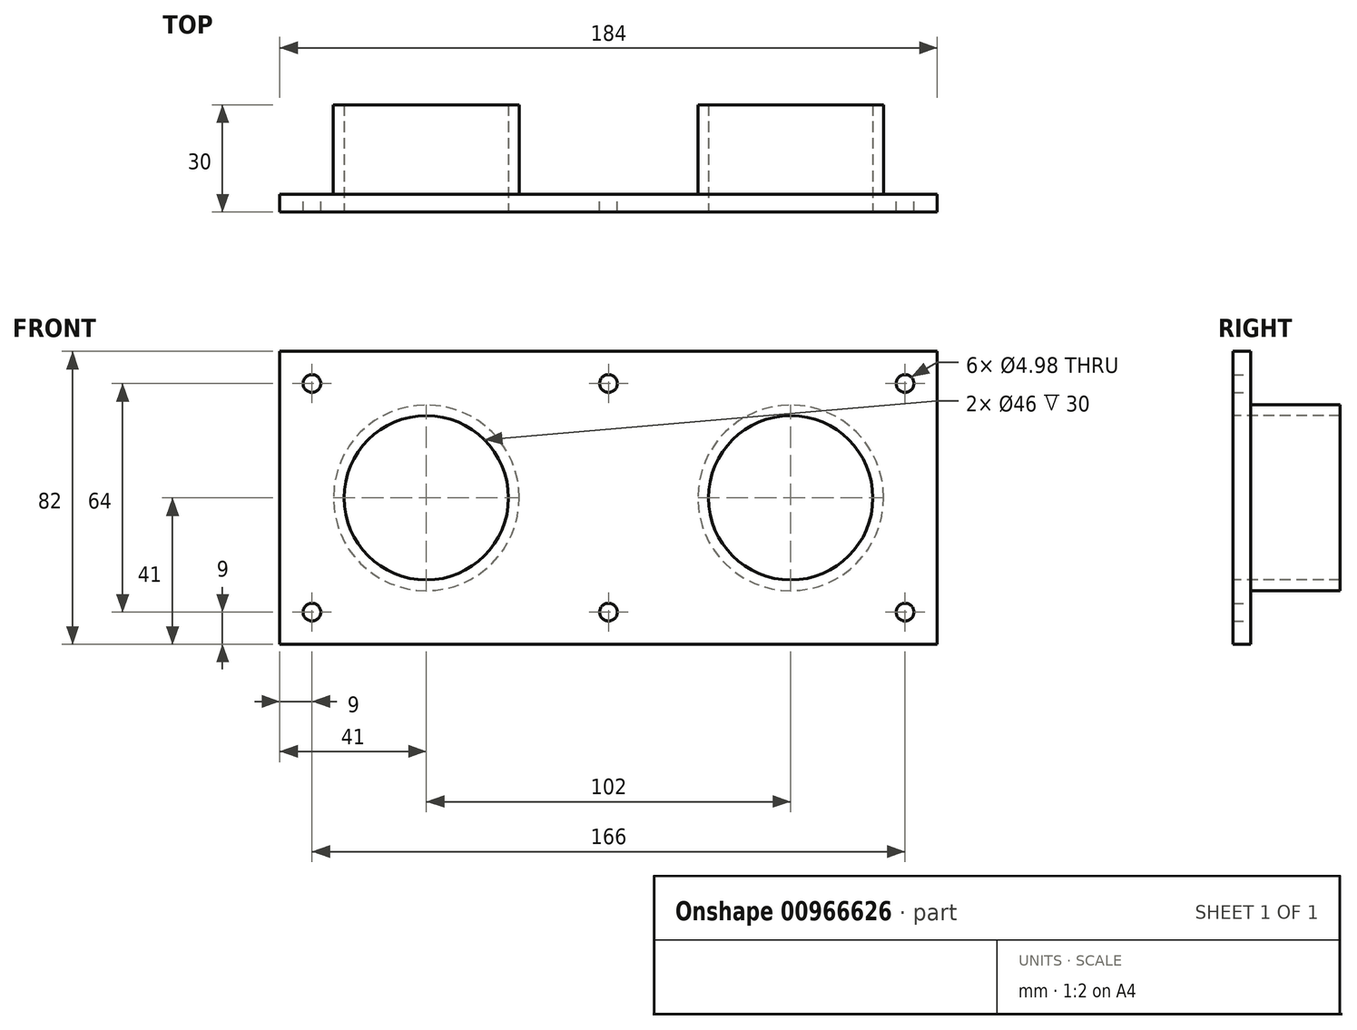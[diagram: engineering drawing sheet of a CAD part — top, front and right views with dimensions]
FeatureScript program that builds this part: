
annotation { "Feature Type Name" : "Feature", "Feature Type Description" : "" }
export const myFeature = defineFeature(function(context is Context, id is Id, definition is map)
    precondition{}
    {
        {
            var Q0;
            Q0=qCreatedBy(makeId("Front.planeOp"),FACE);
            var sketch = newSketch(context, id + "F0", { "sketchPlane" : qUnion([Q0])});
            skCircle(sketch, "E0", {"center": v(-51, 0) * mm, "radius": 26 * mm});
            skCircle(sketch, "E1", {"center": v(51, 0) * mm, "radius": 26 * mm});
            skLineSegment(sketch, "E2", {"start": v(-25, 0) * mm, "end": v(25, 0) * mm, "construction": true});
            skPoint(sketch, "E3", {"position": v(0, 0) * mm});
            skLineSegment(sketch, "E4", {"start": v(-92, 41) * mm, "end": v(-92, -41) * mm});
            skLineSegment(sketch, "E5", {"start": v(-92, -41) * mm, "end": v(92, -41) * mm});
            skLineSegment(sketch, "E6", {"start": v(92, -41) * mm, "end": v(92, 41) * mm});
            skLineSegment(sketch, "E7", {"start": v(92, 41) * mm, "end": v(-92, 41) * mm});
            skCircle(sketch, "E8.0", {"center": v(-51, 0) * mm, "radius": 23 * mm});
            skCircle(sketch, "E9.0", {"center": v(51, 0) * mm, "radius": 23 * mm});
            skSolve(sketch);
        }
        {
            var Q0;
            Q0=makeQuery(id+"F0.imprint","IMPRINT",FACE,{"disambiguationData":[TD([[makeQuery(id+"F0.imprint","IMPRINT",EDGE,{"derivedFrom":sQuery(id+"F0.wireOp",EDGE,"E0")}),-1.0]])]});
            extrude(context, id + "F1", {"entities" : qUnion([Q0]), "depth" : 5 * mm, "offsetDistance" : 25 * mm});
        }
        {
            var Q0;
            Q0=makeQuery(id+"F0.imprint","IMPRINT",FACE,{"disambiguationData":[TD([[makeQuery(id+"F0.imprint","IMPRINT",EDGE,{"derivedFrom":sQuery(id+"F0.wireOp",EDGE,"E0")}),1.0]])]});
            var Q1;
            Q1=makeQuery(id+"F0.imprint","IMPRINT",FACE,{"disambiguationData":[TD([[makeQuery(id+"F0.imprint","IMPRINT",EDGE,{"derivedFrom":sQuery(id+"F0.wireOp",EDGE,"E1")}),1.0]])]});
            extrude(context, id + "F2", {"entities" : qUnion([Q0, Q1]), "operationType" : NewBodyOperationType.ADD, "oppositeDirection" : true, "depth" : 25 * mm, "offsetDistance" : 25 * mm});
        }
        {
            var Q0;
            Q0=makeQuery(id+"F0.imprint","IMPRINT",FACE,{"disambiguationData":[TD([[makeQuery(id+"F0.imprint","IMPRINT",EDGE,{"derivedFrom":sQuery(id+"F0.wireOp",EDGE,"E0")}),1.0]])]});
            var Q1;
            Q1=makeQuery(id+"F0.imprint","IMPRINT",FACE,{"disambiguationData":[TD([[makeQuery(id+"F0.imprint","IMPRINT",EDGE,{"derivedFrom":sQuery(id+"F0.wireOp",EDGE,"E1")}),1.0]])]});
            extrude(context, id + "F3", {"entities" : qUnion([Q0, Q1]), "operationType" : NewBodyOperationType.ADD, "depth" : 5 * mm, "offsetDistance" : 25 * mm});
        }
        {
            var Q0;
            Q0=makeQuery(id+"F0.imprint","IMPRINT",FACE,{"disambiguationData":[TD([[makeQuery(id+"F0.imprint","IMPRINT",EDGE,{"derivedFrom":sQuery(id+"F0.wireOp",EDGE,"E0")}),-1.0]])]});
            var sketch = newSketch(context, id + "F4", { "sketchPlane" : qUnion([Q0])});
            skPoint(sketch, "E10", {"position": v(-83, 32) * mm});
            skPoint(sketch, "E11", {"position": v(-83, -32) * mm});
            skPoint(sketch, "E12", {"position": v(83, 32) * mm});
            skPoint(sketch, "E13", {"position": v(83, -32) * mm});
            skPoint(sketch, "E14", {"position": v(0, 32) * mm});
            skPoint(sketch, "E15", {"position": v(0, -32) * mm});
            skSolve(sketch);
        }
        {
            var Q0;
            Q0=sQuery(id+"F4.wireOp",VERTEX,"E10");
            var Q1;
            Q1=sQuery(id+"F4.wireOp",VERTEX,"E14");
            var Q2;
            Q2=sQuery(id+"F4.wireOp",VERTEX,"E12");
            var Q3;
            Q3=sQuery(id+"F4.wireOp",VERTEX,"E13");
            var Q4;
            Q4=sQuery(id+"F4.wireOp",VERTEX,"E15");
            var Q5;
            Q5=sQuery(id+"F4.wireOp",VERTEX,"E11");
            var Q6;
            Q6=makeQuery(id+"F1.opExtrude","SWEPT_BODY",BODY,{"disambiguationData":[OSD([sQuery(id+"F0.wireOp",EDGE,"E0"),sQuery(id+"F0.wireOp",EDGE,"E1"),sQuery(id+"F0.wireOp",EDGE,"E4"),sQuery(id+"F0.wireOp",EDGE,"E5"),sQuery(id+"F0.wireOp",EDGE,"E6"),sQuery(id+"F0.wireOp",EDGE,"E7")])]});
            hole(context, id + "F5", {"style" : HoleStyle.SIMPLE, "endStyle" : HoleEndStyle.THROUGH, "oppositeDirection" : true, "standardTappedOrClearance" : lookupTablePath({ "fit" : "Normal (ASME)", "standard" : "ANSI", "size" : "#8", "type" : "Clearance" }), "standardBlindInLast" : lookupTablePath({ "fit" : "Normal", "standard" : "ANSI", "engagement" : "75%", "pitch" : "32 tpi", "size" : "#8", "type" : "Clearance & tapped" }), "holeDiameter" : 4.98 * mm, "majorDiameter" : 5 * mm, "isTappedThrough" : true, "tappedDepth" : 4.1 * mm, "tapClearance" : 3, "locations" : qUnion([Q0, Q1, Q2, Q3, Q4, Q5]), "scope" : qUnion([Q6])});
        }
    });
